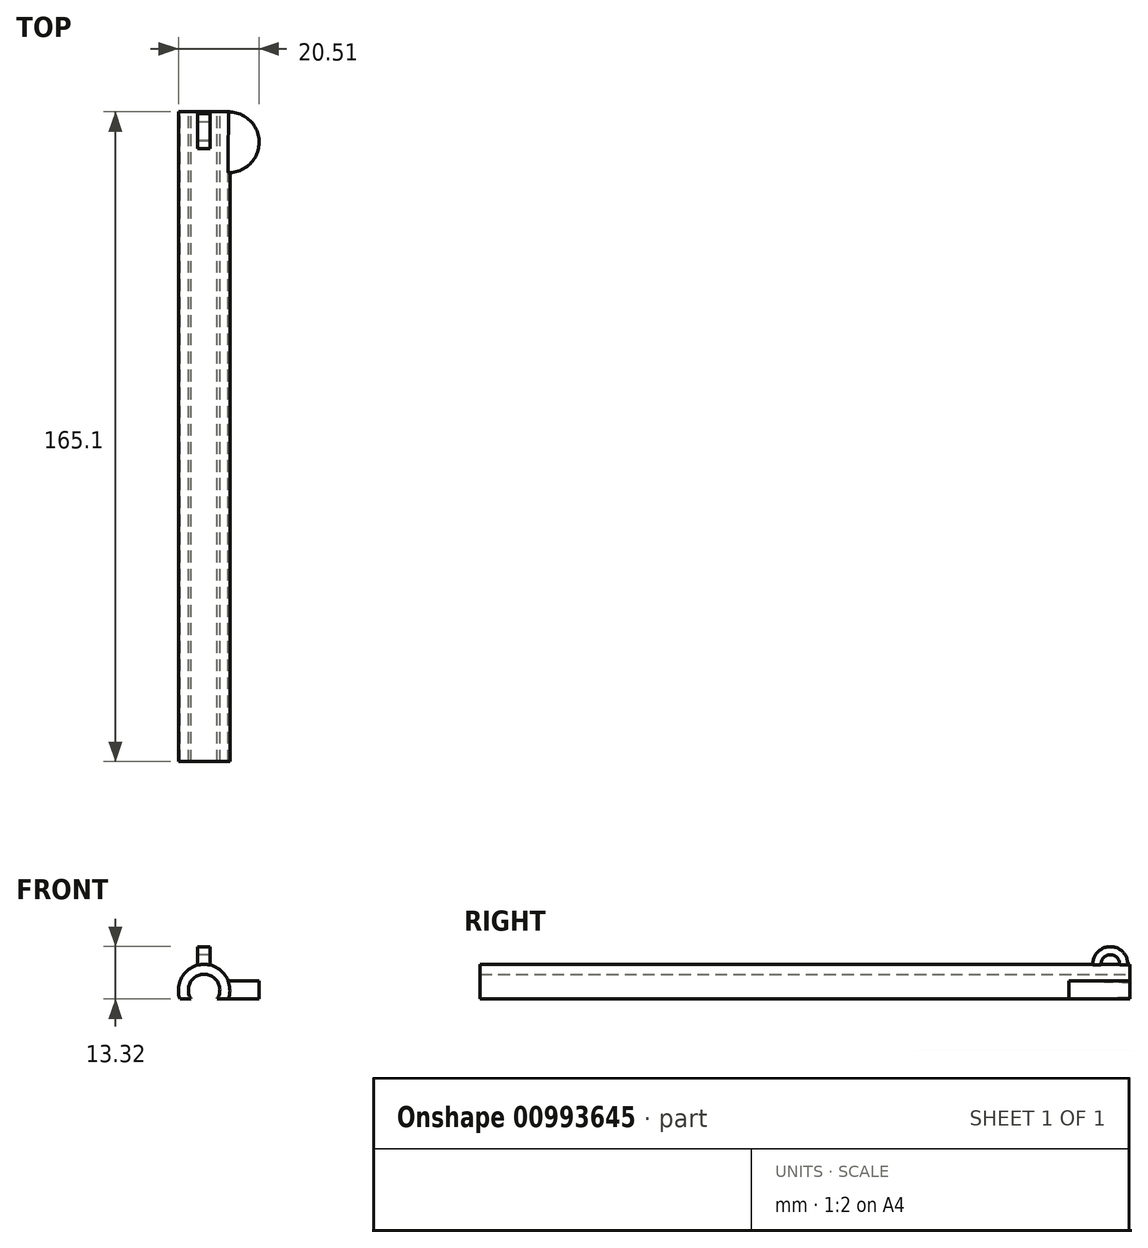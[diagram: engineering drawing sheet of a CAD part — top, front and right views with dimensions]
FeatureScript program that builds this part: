
annotation { "Feature Type Name" : "Feature", "Feature Type Description" : "" }
export const myFeature = defineFeature(function(context is Context, id is Id, definition is map)
    precondition{}
    {
        {
            var Q0;
            Q0=qCreatedBy(makeId("Front.planeOp"),FACE);
            var sketch = newSketch(context, id + "F0", { "sketchPlane" : qUnion([Q0])});
            skArc(sketch, "E0", {"start": v(3.28, -2.28) * mm, "mid": v(0, 4) * mm, "end": v(-3.28, -2.28) * mm});
            skArc(sketch, "E1", {"start": v(6.13, -2.28) * mm, "mid": v(0, 6.54) * mm, "end": v(-6.13, -2.28) * mm});
            skLineSegment(sketch, "E2", {"start": v(-6.13, -2.28) * mm, "end": v(-3.28, -2.28) * mm});
            skLineSegment(sketch, "E3.trimOffspring", {"start": v(3.28, -2.28) * mm, "end": v(6.13, -2.28) * mm});
            skSolve(sketch);
        }
        {
            var Q0;
            {var subQ0=sQuery(id+"F0.wireOp",EDGE,"E0");Q0=makeQuery(id+"F0.imprint","IMPRINT",FACE,{"disambiguationData":[TD([[makeQuery(id+"F0.imprint","IMPRINT",EDGE,{"derivedFrom":subQ0}),-1.0]])]});}
            extrude(context, id + "F1", {"entities" : qUnion([Q0]), "depth" : 165.1 * mm, "offsetDistance" : 25.4 * mm});
        }
        {
            var Q0;
            Q0=qCreatedBy(makeId("Top.planeOp"),FACE);
            var sketch = newSketch(context, id + "F2", { "sketchPlane" : qUnion([Q0])});
            skArc(sketch, "E4", {"start": v(6.1, -15.45) * mm, "mid": v(13.97, -7.8) * mm, "end": v(6.24, 0) * mm});
            skLineSegment(sketch, "E5", {"start": v(6.1, -15.45) * mm, "end": v(6.24, 0) * mm});
            skArc(sketch, "E6.MirrorCS", {"start": v(-6.1, -15.45) * mm, "mid": v(-13.97, -7.8) * mm, "end": v(-6.24, 0) * mm});
            skLineSegment(sketch, "E7", {"start": v(-6.1, -15.45) * mm, "end": v(-6.24, 0) * mm});
            skSolve(sketch);
        }
        {
            var Q0;
            Q0=makeQuery(id+"F2.imprint","IMPRINT",FACE,{"disambiguationData":[TD([[makeQuery(id+"F2.imprint","IMPRINT",EDGE,{"derivedFrom":sQuery(id+"F2.wireOp",EDGE,"E6.MirrorCS")}),-1.0]])]});
            var Q1;
            Q1=makeQuery(id+"F2.imprint","IMPRINT",FACE,{"disambiguationData":[TD([[makeQuery(id+"F2.imprint","IMPRINT",EDGE,{"derivedFrom":sQuery(id+"F2.wireOp",EDGE,"E4")}),1.0]])]});
            extrude(context, id + "F3", {"entities" : qUnion([Q0, Q1]), "operationType" : NewBodyOperationType.ADD, "endBound" : BoundingType.SYMMETRIC, "depth" : 4.57 * mm, "offsetDistance" : 25.4 * mm});
        }
        {
            var Q0;
            Q0=qCreatedBy(makeId("Right.planeOp"),FACE);
            var sketch = newSketch(context, id + "F4", { "sketchPlane" : qUnion([Q0])});
            skArc(sketch, "E8", {"start": v(-2.65, 6.03) * mm, "mid": v(-4.95, 8.97) * mm, "end": v(-7.26, 6.03) * mm});
            skArc(sketch, "E9", {"start": v(-0.54, 6.03) * mm, "mid": v(-4.95, 11.04) * mm, "end": v(-9.36, 6.03) * mm});
            skLineSegment(sketch, "E10", {"start": v(-9.36, 6.03) * mm, "end": v(-7.26, 6.03) * mm});
            skLineSegment(sketch, "E11.trimOffspring", {"start": v(-2.65, 6.03) * mm, "end": v(-0.54, 6.03) * mm});
            skSolve(sketch);
        }
        {
            var Q0;
            Q0=makeQuery(id+"F4.imprint","IMPRINT",FACE,{"disambiguationData":[TD([[makeQuery(id+"F4.imprint","IMPRINT",EDGE,{"derivedFrom":sQuery(id+"F4.wireOp",EDGE,"E8")}),-1.0]])]});
            extrude(context, id + "F5", {"entities" : qUnion([Q0]), "operationType" : NewBodyOperationType.ADD, "endBound" : BoundingType.SYMMETRIC, "depth" : 3.17 * mm, "offsetDistance" : 25.4 * mm});
        }
    });
